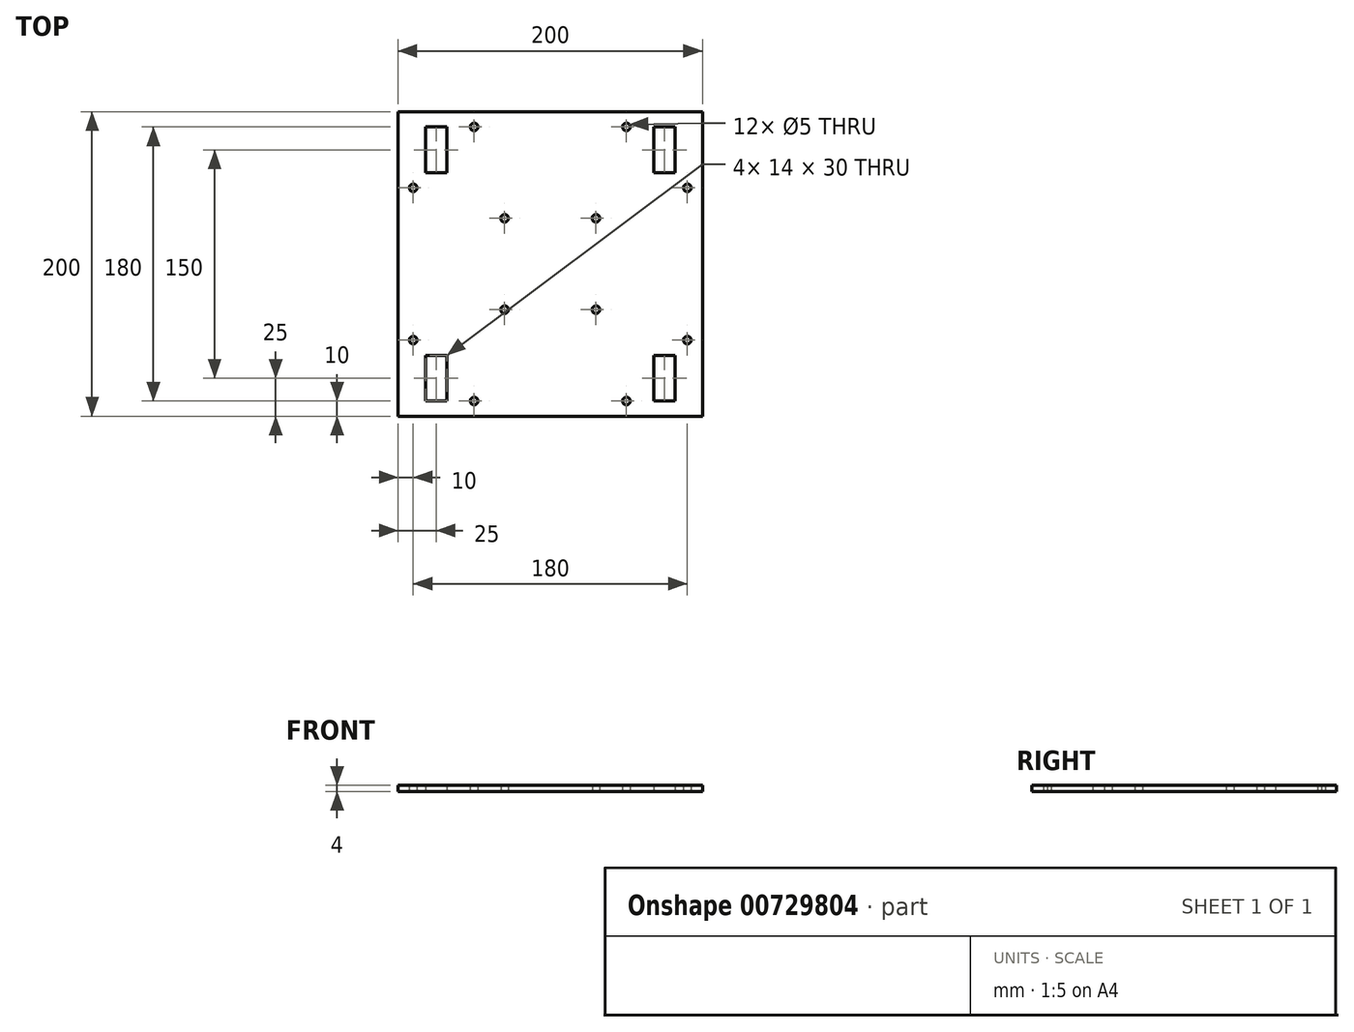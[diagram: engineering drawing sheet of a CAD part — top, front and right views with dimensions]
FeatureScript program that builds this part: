
annotation { "Feature Type Name" : "Feature", "Feature Type Description" : "" }
export const myFeature = defineFeature(function(context is Context, id is Id, definition is map)
    precondition{}
    {
        {
            var Q0;
            Q0=qCreatedBy(makeId("Top.planeOp"),FACE);
            var sketch = newSketch(context, id + "F0", { "sketchPlane" : qUnion([Q0])});
            skLineSegment(sketch, "E0.bottom", {"start": v(100, 100) * mm, "end": v(-100, 100) * mm});
            skLineSegment(sketch, "E0.top", {"start": v(100, -100) * mm, "end": v(-100, -100) * mm});
            skLineSegment(sketch, "E0.left", {"start": v(100, 100) * mm, "end": v(100, -100) * mm});
            skLineSegment(sketch, "E0.right", {"start": v(-100, 100) * mm, "end": v(-100, -100) * mm});
            skPoint(sketch, "E0.middle", {"position": v(0, 0) * mm});
            skLineSegment(sketch, "E1.bottom", {"start": v(-75, -75) * mm, "end": v(75, -75) * mm, "construction": true});
            skLineSegment(sketch, "E1.top", {"start": v(-75, 75) * mm, "end": v(75, 75) * mm, "construction": true});
            skLineSegment(sketch, "E1.left", {"start": v(-75, -75) * mm, "end": v(-75, 75) * mm, "construction": true});
            skLineSegment(sketch, "E1.right", {"start": v(75, -75) * mm, "end": v(75, 75) * mm, "construction": true});
            skLineSegment(sketch, "E2.bottom", {"start": v(82, 60) * mm, "end": v(68, 60) * mm});
            skLineSegment(sketch, "E2.top", {"start": v(82, 90) * mm, "end": v(68, 90) * mm});
            skLineSegment(sketch, "E2.left", {"start": v(82, 60) * mm, "end": v(82, 90) * mm});
            skLineSegment(sketch, "E2.right", {"start": v(68, 60) * mm, "end": v(68, 90) * mm});
            skPoint(sketch, "E2.middle", {"position": v(75, 75) * mm});
            skLineSegment(sketch, "E3.bottom", {"start": v(68, -60) * mm, "end": v(82, -60) * mm});
            skLineSegment(sketch, "E3.top", {"start": v(68, -90) * mm, "end": v(82, -90) * mm});
            skLineSegment(sketch, "E3.left", {"start": v(68, -60) * mm, "end": v(68, -90) * mm});
            skLineSegment(sketch, "E3.right", {"start": v(82, -60) * mm, "end": v(82, -90) * mm});
            skPoint(sketch, "E3.middle", {"position": v(75, -75) * mm});
            skLineSegment(sketch, "E4.bottom", {"start": v(-82, -90) * mm, "end": v(-68, -90) * mm});
            skLineSegment(sketch, "E4.top", {"start": v(-82, -60) * mm, "end": v(-68, -60) * mm});
            skLineSegment(sketch, "E4.left", {"start": v(-82, -90) * mm, "end": v(-82, -60) * mm});
            skLineSegment(sketch, "E4.right", {"start": v(-68, -90) * mm, "end": v(-68, -60) * mm});
            skPoint(sketch, "E4.middle", {"position": v(-75, -75) * mm});
            skLineSegment(sketch, "E5.bottom", {"start": v(-68, 60) * mm, "end": v(-82, 60) * mm});
            skLineSegment(sketch, "E5.top", {"start": v(-68, 90) * mm, "end": v(-82, 90) * mm});
            skLineSegment(sketch, "E5.left", {"start": v(-68, 60) * mm, "end": v(-68, 90) * mm});
            skLineSegment(sketch, "E5.right", {"start": v(-82, 60) * mm, "end": v(-82, 90) * mm});
            skPoint(sketch, "E5.middle", {"position": v(-75, 75) * mm});
            skLineSegment(sketch, "E6.bottom", {"start": v(-50, -90) * mm, "end": v(50, -90) * mm, "construction": true});
            skLineSegment(sketch, "E6.top", {"start": v(-50, 90) * mm, "end": v(50, 90) * mm, "construction": true});
            skLineSegment(sketch, "E6.left", {"start": v(-50, -90) * mm, "end": v(-50, 90) * mm, "construction": true});
            skLineSegment(sketch, "E6.right", {"start": v(50, -90) * mm, "end": v(50, 90) * mm, "construction": true});
            skCircle(sketch, "E7", {"center": v(-50, 90) * mm, "radius": 2.5 * mm});
            skCircle(sketch, "E8", {"center": v(50, 90) * mm, "radius": 2.5 * mm});
            skCircle(sketch, "E9", {"center": v(-50, -90) * mm, "radius": 2.5 * mm});
            skCircle(sketch, "E10", {"center": v(50, -90) * mm, "radius": 2.5 * mm});
            skLineSegment(sketch, "E11.bottom", {"start": v(90, 50) * mm, "end": v(-90, 50) * mm, "construction": true});
            skLineSegment(sketch, "E11.top", {"start": v(90, -50) * mm, "end": v(-90, -50) * mm, "construction": true});
            skLineSegment(sketch, "E11.left", {"start": v(90, 50) * mm, "end": v(90, -50) * mm, "construction": true});
            skLineSegment(sketch, "E11.right", {"start": v(-90, 50) * mm, "end": v(-90, -50) * mm, "construction": true});
            skCircle(sketch, "E12", {"center": v(-90, 50) * mm, "radius": 2.5 * mm});
            skCircle(sketch, "E13", {"center": v(90, 50) * mm, "radius": 2.5 * mm});
            skCircle(sketch, "E14", {"center": v(90, -50) * mm, "radius": 2.5 * mm});
            skCircle(sketch, "E15", {"center": v(-90, -50) * mm, "radius": 2.5 * mm});
            skLineSegment(sketch, "E16.bottom", {"start": v(30, 30) * mm, "end": v(-30, 30) * mm, "construction": true});
            skLineSegment(sketch, "E16.top", {"start": v(30, -30) * mm, "end": v(-30, -30) * mm, "construction": true});
            skLineSegment(sketch, "E16.left", {"start": v(30, 30) * mm, "end": v(30, -30) * mm, "construction": true});
            skLineSegment(sketch, "E16.right", {"start": v(-30, 30) * mm, "end": v(-30, -30) * mm, "construction": true});
            skCircle(sketch, "E17", {"center": v(-30, 30) * mm, "radius": 2.5 * mm});
            skCircle(sketch, "E18", {"center": v(30, 30) * mm, "radius": 2.5 * mm});
            skCircle(sketch, "E19", {"center": v(-30, -30) * mm, "radius": 2.5 * mm});
            skCircle(sketch, "E20", {"center": v(30, -30) * mm, "radius": 2.5 * mm});
            skSolve(sketch);
        }
        {
            var Q0;
            Q0 = qSketchRegion(id + "F0", true);
            extrude(context, id + "F1", {"entities" : qUnion([Q0]), "depth" : 4 * mm, "offsetDistance" : 25 * mm});
        }
    });
